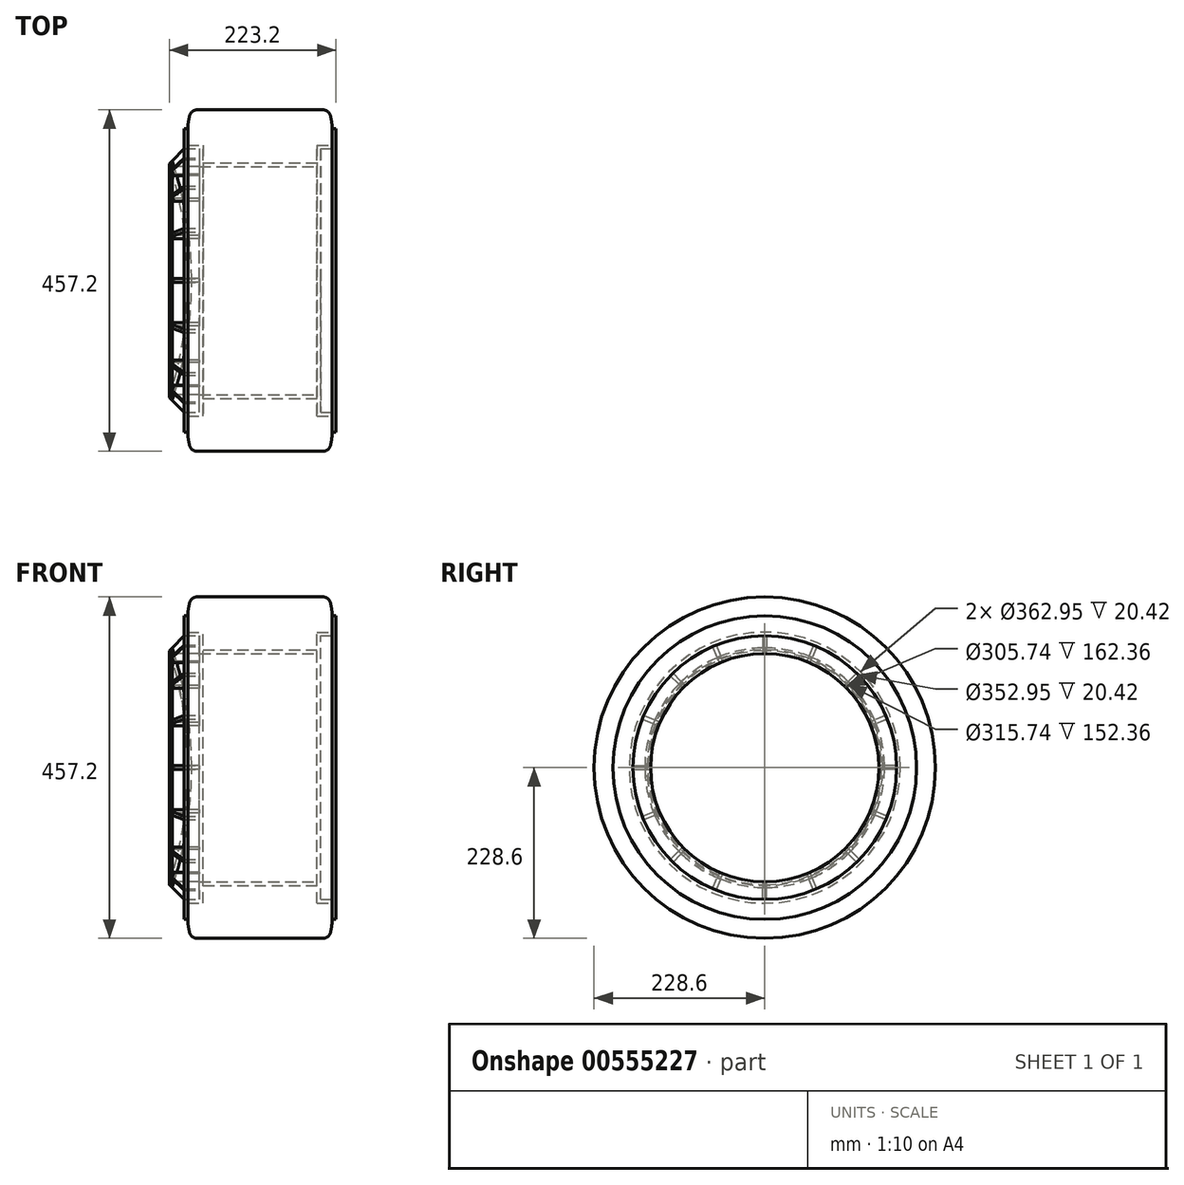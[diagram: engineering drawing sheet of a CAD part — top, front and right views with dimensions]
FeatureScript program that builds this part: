
annotation { "Feature Type Name" : "Feature", "Feature Type Description" : "" }
export const myFeature = defineFeature(function(context is Context, id is Id, definition is map)
    precondition{}
    {
        {
            var Q0;
            Q0=qCreatedBy(makeId("Front.planeOp"),FACE);
            var sketch = newSketch(context, id + "F0", { "sketchPlane" : qUnion([Q0])});
            skLineSegment(sketch, "E0.bottom", {"start": v(101.6, 203.2) * mm, "end": v(-101.6, 203.2) * mm, "construction": true});
            skLineSegment(sketch, "E0.top", {"start": v(101.6, -203.2) * mm, "end": v(-101.6, -203.2) * mm, "construction": true});
            skLineSegment(sketch, "E0.left", {"start": v(101.6, 203.2) * mm, "end": v(101.6, -203.2) * mm, "construction": true});
            skLineSegment(sketch, "E0.right", {"start": v(-101.6, 203.2) * mm, "end": v(-101.6, -203.2) * mm, "construction": true});
            skPoint(sketch, "E0.middle", {"position": v(0, 0) * mm});
            skLineSegment(sketch, "E1", {"start": v(0, 0) * mm, "end": v(0, 203.2) * mm, "construction": true});
            skLineSegment(sketch, "E2.MirrorCS", {"start": v(-101.6, 203.2) * mm, "end": v(-101.6, 176.48) * mm});
            skLineSegment(sketch, "E3.MirrorCS", {"start": v(-101.6, 176.48) * mm, "end": v(-81.18, 176.48) * mm});
            skPoint(sketch, "E4.MirrorP", {"position": v(-101.6, 176.48) * mm});
            skLineSegment(sketch, "E5", {"start": v(-101.6, 176.48) * mm, "end": v(-117.64, 160.43) * mm, "construction": true});
            skLineSegment(sketch, "E6", {"start": v(-96.6, 0) * mm, "end": v(-96.6, 203.2) * mm, "construction": true});
            skLineSegment(sketch, "E7.MirrorCS", {"start": v(-96.6, 0) * mm, "end": v(-96.6, -203.2) * mm, "construction": true});
            skArc(sketch, "E8", {"start": v(-96.6, 0) * mm, "mid": v(-102.89, 79.23) * mm, "end": v(-121.6, 156.48) * mm});
            skArc(sketch, "E9.0", {"start": v(-91.6, 0) * mm, "mid": v(-98.15, 81.27) * mm, "end": v(-117.64, 160.43) * mm});
            skLineSegment(sketch, "E10", {"start": v(-91.6, 0) * mm, "end": v(-96.6, 0) * mm});
            skLineSegment(sketch, "E11", {"start": v(0, 0) * mm, "end": v(-96.6, 0) * mm, "construction": true});
            skLineSegment(sketch, "E12", {"start": v(-121.6, 156.48) * mm, "end": v(-117.64, 160.43) * mm});
            skLineSegment(sketch, "E13", {"start": v(-81.18, 176.48) * mm, "end": v(-81.18, 152.87) * mm});
            skLineSegment(sketch, "E14", {"start": v(-81.18, 152.87) * mm, "end": v(0, 152.87) * mm});
            skLineSegment(sketch, "E15.0", {"start": v(-76.18, 157.87) * mm, "end": v(0, 157.87) * mm});
            skLineSegment(sketch, "E15.1", {"start": v(-76.18, 181.48) * mm, "end": v(-76.18, 157.87) * mm});
            skLineSegment(sketch, "E15.2", {"start": v(-96.6, 181.48) * mm, "end": v(-76.18, 181.48) * mm});
            skLineSegment(sketch, "E15.3", {"start": v(-96.6, 206.9) * mm, "end": v(-96.6, 181.48) * mm});
            skLineSegment(sketch, "E16", {"start": v(-96.6, 203.2) * mm, "end": v(-101.6, 203.2) * mm});
            skLineSegment(sketch, "E17.MirrorCS", {"start": v(96.6, 203.2) * mm, "end": v(101.6, 203.2) * mm});
            skLineSegment(sketch, "E18.MirrorCS", {"start": v(96.6, 181.48) * mm, "end": v(76.18, 181.48) * mm});
            skLineSegment(sketch, "E19.MirrorCS", {"start": v(101.6, 176.48) * mm, "end": v(81.18, 176.48) * mm});
            skLineSegment(sketch, "E20.MirrorCS", {"start": v(101.6, 203.2) * mm, "end": v(101.6, 176.48) * mm});
            skLineSegment(sketch, "E21.MirrorCS", {"start": v(96.6, 206.9) * mm, "end": v(96.6, 181.48) * mm});
            skLineSegment(sketch, "E22.MirrorCS", {"start": v(76.18, 181.48) * mm, "end": v(76.18, 157.87) * mm});
            skLineSegment(sketch, "E23.MirrorCS", {"start": v(76.18, 157.87) * mm, "end": v(0, 157.87) * mm});
            skLineSegment(sketch, "E24.MirrorCS", {"start": v(81.18, 176.48) * mm, "end": v(81.18, 152.87) * mm});
            skLineSegment(sketch, "E25.MirrorCS", {"start": v(81.18, 152.87) * mm, "end": v(0, 152.87) * mm});
            skPoint(sketch, "E26.MirrorP", {"position": v(101.6, 176.48) * mm});
            skLineSegment(sketch, "E27", {"start": v(-81.18, 152.87) * mm, "end": v(-115.19, 152.87) * mm, "construction": true});
            skSolve(sketch);
        }
        {
            var Q0;
            Q0=qSketchRegion(id+"F0",true);
            var Q1;
            Q1=sQuery(id+"F0.wireOp",EDGE,"E11");
            revolve(context, id + "F1", {"entities" : qUnion([Q0]), "axis" : qUnion([Q1]), "revolveType" : RevolveType.FULL});
        }
        {
            var Q0;
            Q0=qCreatedBy(makeId("Front.planeOp"),FACE);
            var sketch = newSketch(context, id + "F2", { "sketchPlane" : qUnion([Q0])});
            skLineSegment(sketch, "E28.0", {"start": v(-101.6, 176.48) * mm, "end": v(-117.64, 160.43) * mm});
            skLineSegment(sketch, "E29.0", {"start": v(-81.18, 152.87) * mm, "end": v(-115.19, 152.87) * mm});
            skArc(sketch, "E30.0", {"start": v(-91.6, 0) * mm, "mid": v(-98.15, 81.27) * mm, "end": v(-117.64, 160.43) * mm});
            skLineSegment(sketch, "E31.0", {"start": v(-81.18, 176.48) * mm, "end": v(-81.18, 152.87) * mm});
            skPoint(sketch, "E32.0", {"position": v(-91.39, 176.48) * mm});
            skLineSegment(sketch, "E33.0", {"start": v(-101.6, 176.48) * mm, "end": v(-81.18, 176.48) * mm});
            skSolve(sketch);
        }
        {
            var Q0;
            Q0=qSketchRegion(id+"F2",true);
            extrude(context, id + "F3", {"entities" : qUnion([Q0]), "endBound" : BoundingType.SYMMETRIC, "depth" : 5 * mm, "offsetDistance" : 25 * mm});
        }
        {
            var Q0;
            Q0=makeQuery(id+"F3.opExtrude","SWEPT_BODY",BODY,{"disambiguationData":[OSD([sQuery(id+"F2.wireOp",EDGE,"E28.0"),sQuery(id+"F2.wireOp",EDGE,"E29.0"),sQuery(id+"F2.wireOp",EDGE,"E30.0"),sQuery(id+"F2.wireOp",EDGE,"E31.0"),sQuery(id+"F2.wireOp",EDGE,"E33.0")])]});
            var Q1;
            Q1=sQuery(id+"F0.wireOp",EDGE,"E11");
            circularPattern(context, id + "F4", {"operationType" : NewBodyOperationType.ADD, "entities" : qUnion([Q0]), "axis" : qUnion([Q1]), "angle" : 360 * degree, "instanceCount" : 16, "equalSpace" : true});
        }
        {
            var Q0;
            Q0=qCreatedBy(makeId("Front.planeOp"),FACE);
            var sketch = newSketch(context, id + "F5", { "sketchPlane" : qUnion([Q0])});
            skLineSegment(sketch, "E34", {"start": v(76.18, 157.87) * mm, "end": v(-76.18, 157.87) * mm});
            skLineSegment(sketch, "E35", {"start": v(-76.18, -157.87) * mm, "end": v(76.18, -157.87) * mm, "construction": true});
            skLineSegment(sketch, "E36", {"start": v(-76.18, -157.87) * mm, "end": v(-76.18, -181.48) * mm, "construction": true});
            skLineSegment(sketch, "E37", {"start": v(-76.18, 181.48) * mm, "end": v(-76.18, 157.87) * mm});
            skLineSegment(sketch, "E38", {"start": v(-96.6, 181.48) * mm, "end": v(-76.18, 181.48) * mm});
            skLineSegment(sketch, "E39", {"start": v(-76.18, -181.48) * mm, "end": v(-96.6, -181.48) * mm, "construction": true});
            skLineSegment(sketch, "E40", {"start": v(-96.6, -181.48) * mm, "end": v(-96.6, -203.2) * mm, "construction": true});
            skLineSegment(sketch, "E41", {"start": v(-96.6, 203.2) * mm, "end": v(-96.6, 181.48) * mm});
            skLineSegment(sketch, "E42", {"start": v(-96.6, 203.2) * mm, "end": v(-101.6, 203.2) * mm});
            skLineSegment(sketch, "E43", {"start": v(-101.6, -203.2) * mm, "end": v(-96.6, -203.2) * mm, "construction": true});
            skLineSegment(sketch, "E44", {"start": v(0, 228.6) * mm, "end": v(0, -26.01) * mm, "construction": true});
            skLineSegment(sketch, "E45", {"start": v(0, 280.44) * mm, "end": v(0, -26.01) * mm, "construction": true});
            skLineSegment(sketch, "E46", {"start": v(0, 228.6) * mm, "end": v(-84.48, 228.6) * mm});
            skArc(sketch, "E47", {"start": v(-96.6, 203.2) * mm, "mid": v(-95.97, 212.34) * mm, "end": v(-94.1, 221.3) * mm});
            skPoint(sketch, "E48.visualSharp", {"position": v(-91.6, 228.6) * mm});
            skArc(sketch, "E48.filletArc", {"start": v(-84.48, 228.6) * mm, "mid": v(-90.52, 226.57) * mm, "end": v(-94.1, 221.3) * mm});
            skArc(sketch, "E49.MirrorCS", {"start": v(84.48, 228.6) * mm, "mid": v(90.52, 226.57) * mm, "end": v(94.1, 221.3) * mm});
            skLineSegment(sketch, "E50.MirrorCS", {"start": v(96.6, 203.2) * mm, "end": v(101.6, 203.2) * mm});
            skArc(sketch, "E51.MirrorCS", {"start": v(96.6, 203.2) * mm, "mid": v(95.97, 212.34) * mm, "end": v(94.1, 221.3) * mm});
            skPoint(sketch, "E52.MirrorP", {"position": v(91.6, 228.6) * mm});
            skLineSegment(sketch, "E53.MirrorCS", {"start": v(0, 228.6) * mm, "end": v(84.48, 228.6) * mm});
            skLineSegment(sketch, "E54.MirrorCS", {"start": v(96.6, 181.48) * mm, "end": v(76.18, 181.48) * mm});
            skLineSegment(sketch, "E55.MirrorCS", {"start": v(96.6, 203.2) * mm, "end": v(96.6, 181.48) * mm});
            skLineSegment(sketch, "E56.MirrorCS", {"start": v(76.18, 181.48) * mm, "end": v(76.18, 157.87) * mm});
            skSolve(sketch);
        }
        {
            var Q0;
            Q0=qSketchRegion(id+"F5",true);
            var Q1;
            Q1=sQuery(id+"F0.wireOp",EDGE,"E11");
            revolve(context, id + "F6", {"entities" : qUnion([Q0]), "axis" : qUnion([Q1]), "revolveType" : RevolveType.FULL});
        }
        {
            var Q0;
            Q0=qCreatedBy(makeId("Right.planeOp"),FACE);
            cPlane(context, id + "F7", {"entities" : qUnion([Q0]), "cplaneType" : CPlaneType.OFFSET, "offset" : 141 * mm, "width" : 150 * mm, "height" : 150 * mm});
        }
        {
            var Q0;
            Q0=qCreatedBy(id+"F7.planeOp",FACE);
            var sketch = newSketch(context, id + "F8", { "sketchPlane" : qUnion([Q0])});
            skPoint(sketch, "E57.0", {"position": v(0, 0) * mm});
            skSolve(sketch);
        }
    });
